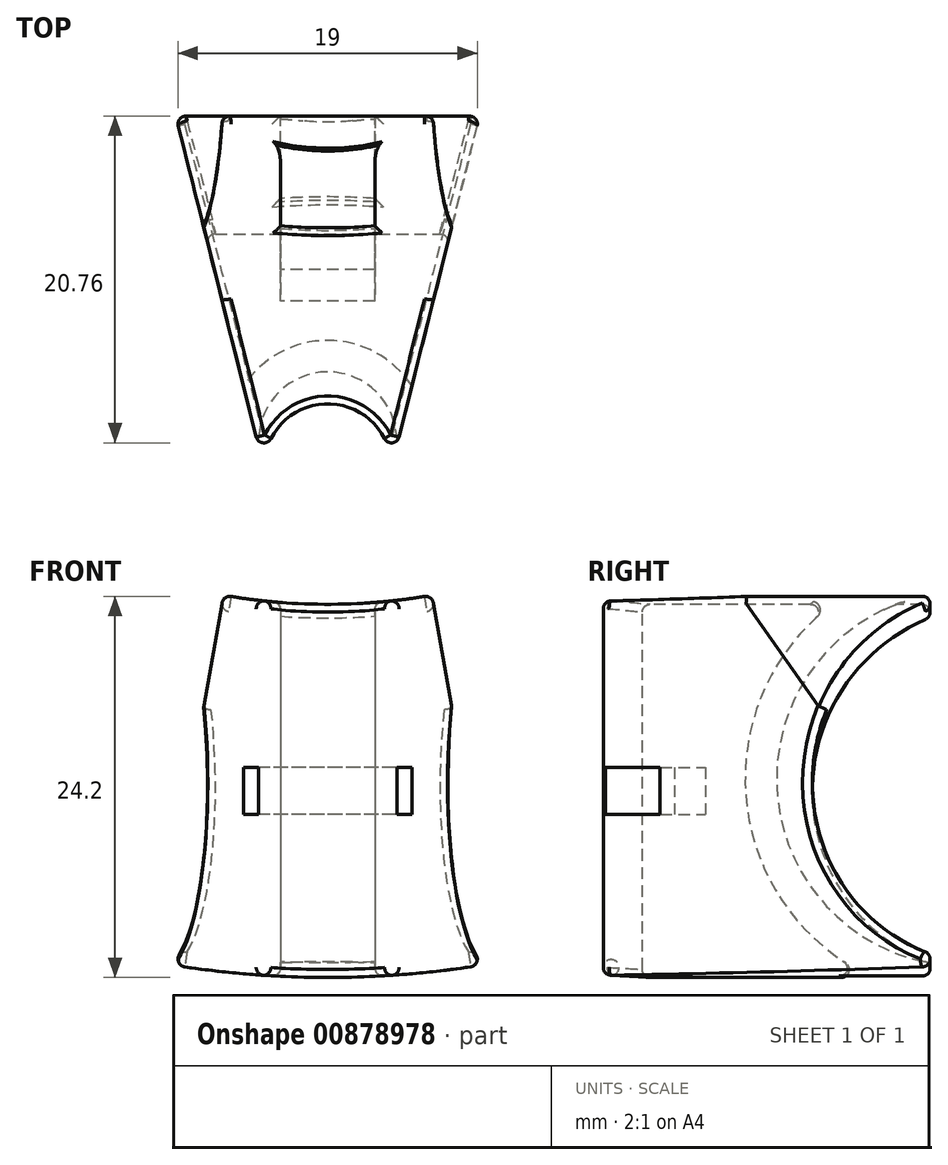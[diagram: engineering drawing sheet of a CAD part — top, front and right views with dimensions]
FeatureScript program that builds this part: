
annotation { "Feature Type Name" : "Feature", "Feature Type Description" : "" }
export const myFeature = defineFeature(function(context is Context, id is Id, definition is map)
    precondition{}
    {
        {
            var Q0;
            Q0=qCreatedBy(makeId("Right.planeOp"),FACE);
            var sketch = newSketch(context, id + "F0", { "sketchPlane" : qUnion([Q0])});
            skLineSegment(sketch, "E0", {"start": v(0, 0) * mm, "end": v(12.73, 0) * mm});
            skLineSegment(sketch, "E1.0", {"start": v(0, -50) * mm, "end": v(12.73, -50) * mm});
            skArc(sketch, "E2", {"start": v(0, -38.15) * mm, "mid": v(-11.85, -50) * mm, "end": v(0, -61.85) * mm});
            skLineSegment(sketch, "E3", {"start": v(0, -38.15) * mm, "end": v(-26.7, -38.15) * mm});
            skLineSegment(sketch, "E4", {"start": v(0, -61.85) * mm, "end": v(-26.7, -61.85) * mm});
            skLineSegment(sketch, "E5", {"start": v(-26.7, -38.15) * mm, "end": v(-26.7, -61.85) * mm});
            skSolve(sketch);
        }
        {
            var Q0;
            Q0 = qSketchRegion(id + "F0", true);
            var Q1;
            Q1=sQuery(id+"F0.wireOp",EDGE,"E0");
            revolve(context, id + "F1", {"surfaceOperationType" : NewSurfaceOperationType.NEW, "entities" : qUnion([Q0]), "axis" : qUnion([Q1]), "revolveType" : RevolveType.SYMMETRIC, "angle" : 20 * degree});
        }
        {
            var Q0;
            Q0=qCreatedBy(makeId("Top.planeOp"),FACE);
            var sketch = newSketch(context, id + "F2", { "sketchPlane" : qUnion([Q0])});
            skLineSegment(sketch, "E6.0", {"start": v(-10.74, -26.7) * mm, "end": v(10.74, -26.7) * mm});
            skCircle(sketch, "E7", {"center": v(0, -26.7) * mm, "radius": 4.05 * mm});
            skSolve(sketch);
        }
        {
            var Q0;
            Q0 = qSketchRegion(id + "F2", true);
            extrude(context, id + "F3", {"entities" : qUnion([Q0]), "operationType" : NewBodyOperationType.REMOVE, "endBound" : BoundingType.THROUGH_ALL, "oppositeDirection" : true, "depth" : 25 * mm, "offsetDistance" : 25 * mm});
        }
        {
            var Q0;
            Q0=qCreatedBy(makeId("Top.planeOp"),FACE);
            var sketch = newSketch(context, id + "F4", { "sketchPlane" : qUnion([Q0])});
            skLineSegment(sketch, "E8.0", {"start": v(-10.74, 0) * mm, "end": v(10.74, 0) * mm});
            skLineSegment(sketch, "E9.0", {"start": v(-10.74, -26.7) * mm, "end": v(-4.05, -26.7) * mm});
            skLineSegment(sketch, "E10.0", {"start": v(4.05, -26.7) * mm, "end": v(10.74, -26.7) * mm});
            skLineSegment(sketch, "E11", {"start": v(-10.74, 0) * mm, "end": v(-4.05, -26.7) * mm});
            skLineSegment(sketch, "E12", {"start": v(4.05, -26.7) * mm, "end": v(10.74, 0) * mm});
            skLineSegment(sketch, "E13", {"start": v(10.74, 0) * mm, "end": v(18.67, 0) * mm});
            skLineSegment(sketch, "E14", {"start": v(18.67, 0) * mm, "end": v(18.67, -26.7) * mm});
            skLineSegment(sketch, "E15", {"start": v(18.67, -26.7) * mm, "end": v(7.4, -26.7) * mm});
            skLineSegment(sketch, "E16", {"start": v(7.4, -26.7) * mm, "end": v(4.05, -26.7) * mm});
            skLineSegment(sketch, "E17", {"start": v(-4.05, -26.7) * mm, "end": v(-16.2, -26.7) * mm});
            skLineSegment(sketch, "E18", {"start": v(-16.2, -26.7) * mm, "end": v(-16.2, 0) * mm});
            skLineSegment(sketch, "E19", {"start": v(-16.2, 0) * mm, "end": v(-10.74, 0) * mm});
            skSolve(sketch);
        }
        {
            var Q0;
            Q0 = qSketchRegion(id + "F4", true);
            extrude(context, id + "F5", {"entities" : qUnion([Q0]), "operationType" : NewBodyOperationType.REMOVE, "endBound" : BoundingType.THROUGH_ALL, "oppositeDirection" : true, "depth" : 25 * mm, "offsetDistance" : 25 * mm});
        }
        {
            var Q0;
            Q0=qCreatedBy(makeId("Right.planeOp"),FACE);
            var sketch = newSketch(context, id + "F6", { "sketchPlane" : qUnion([Q0])});
            skFitSpline(sketch, "E20.0", {"points": [v(0, -60.91) * mm, v(-0.47, -60.93) * mm, v(-1.4, -60.91) * mm, v(-2.56, -60.75) * mm, v(-3.47, -60.54) * mm, v(-4.38, -60.26) * mm, v(-5.46, -59.82) * mm, v(-6.69, -59.13) * mm, v(-7.84, -58.27) * mm, v(-8.86, -57.29) * mm, v(-9.6, -56.36) * mm, v(-10.13, -55.56) * mm, v(-10.6, -54.73) * mm, v(-11, -53.86) * mm, v(-11.32, -52.95) * mm, v(-11.51, -52.25) * mm, v(-11.66, -51.54) * mm, v(-11.8, -50.59) * mm, v(-11.86, -49.63) * mm, v(-11.84, -48.66) * mm, v(-11.75, -47.7) * mm, v(-11.54, -46.51) * mm, v(-11.26, -45.6) * mm, v(-11.1, -45.14) * mm]});
            skEllipticalArc(sketch, "E21.0", {});
            skArc(sketch, "E22", {"start": v(0, -37.57) * mm, "mid": v(-14.12, -49.24) * mm, "end": v(0, -60.91) * mm});
            skArc(sketch, "E23.0", {"start": v(0.38, -35.6) * mm, "mid": v(-16.12, -49.24) * mm, "end": v(0.38, -62.87) * mm});
            skLineSegment(sketch, "E24", {"start": v(0, -60.91) * mm, "end": v(0.38, -62.87) * mm});
            skLineSegment(sketch, "E25", {"start": v(0, -37.57) * mm, "end": v(0.38, -35.6) * mm});
            const initialGuessF6  = {"E21.0": [0, -0.0492403876506104, 1, 0, 0.01185, 0.011669971873194664, 1.5707963267948966, 2.7827175404748377]};
            skSetInitialGuess(sketch, initialGuessF6);
            skSolve(sketch);
        }
        {
            var Q0;
            Q0=makeQuery(id+"F6.imprint","IMPRINT",FACE,{"disambiguationData":[TD([[makeQuery(id+"F6.imprint","IMPRINT",EDGE,{"derivedFrom":sQuery(id+"F6.wireOp",EDGE,"E22")}),-1.0]])]});
            var Q1;
            Q1=sQuery(id+"F6.wireOp",EDGE,"E23.0");
            var Q2;
            Q2=sQuery(id+"F6.wireOp",EDGE,"E22");
            var Q3;
            Q3=sQuery(id+"F6.wireOp",EDGE,"E24");
            var Q4;
            Q4=sQuery(id+"F6.wireOp",EDGE,"E25");
            extrude(context, id + "F7", {"entities" : qUnion([Q0]), "operationType" : NewBodyOperationType.REMOVE, "surfaceEntities" : qUnion([Q1, Q2, Q3, Q4]), "endBound" : BoundingType.SYMMETRIC, "depth" : 6 * mm, "offsetDistance" : 25 * mm});
        }
        {
            var Q0;
            Q0=qCreatedBy(makeId("Top.planeOp"),FACE);
            cPlane(context, id + "F8", {"entities" : qUnion([Q0]), "cplaneType" : CPlaneType.OFFSET, "offset" : 50 * mm, "oppositeDirection" : true, "width" : 150 * mm, "height" : 150 * mm});
        }
        {
            var Q0;
            Q0=qCreatedBy(id+"F8.planeOp",FACE);
            var sketch = newSketch(context, id + "F9", { "sketchPlane" : qUnion([Q0])});
            skArc(sketch, "E26.0", {"start": v(4.05, -26.7) * mm, "mid": v(0, -22.65) * mm, "end": v(-4.05, -26.7) * mm});
            skArc(sketch, "E27", {"start": v(4.05, -26.7) * mm, "mid": v(0, -20.62) * mm, "end": v(-4.05, -26.7) * mm});
            skArc(sketch, "E28.0", {"start": v(5.9, -27.47) * mm, "mid": v(0, -18.62) * mm, "end": v(-5.9, -27.47) * mm});
            skLineSegment(sketch, "E29", {"start": v(-4.05, -26.7) * mm, "end": v(-5.9, -27.47) * mm});
            skLineSegment(sketch, "E30", {"start": v(4.05, -26.7) * mm, "end": v(5.9, -27.47) * mm});
            skSolve(sketch);
        }
        {
            var Q0;
            Q0=makeQuery(id+"F9.imprint","IMPRINT",FACE,{"disambiguationData":[TD([[makeQuery(id+"F9.imprint","IMPRINT",EDGE,{"derivedFrom":sQuery(id+"F9.wireOp",EDGE,"E27")}),-1.0]])]});
            extrude(context, id + "F10", {"entities" : qUnion([Q0]), "operationType" : NewBodyOperationType.REMOVE, "endBound" : BoundingType.SYMMETRIC, "depth" : 3 * mm, "offsetDistance" : 25 * mm});
        }
        {
            var Q0;
            Q0=makeQuery(id+"F1.opRevolve","SWEPT_FACE",FACE,{"disambiguationData":[OSD([sQuery(id+"F0.wireOp",EDGE,"E3")])]});
            fillet(context, id + "F11", {"entities" : qUnion([Q0]), "tangentPropagation" : true, "radius" : 0.5 * mm, "defaultsChanged" : true, "vertexSettings" : [], "allowEdgeOverflow" : false});
        }
        {
            var Q0;
            Q0=makeQuery(id+"F1.opRevolve","SWEPT_FACE",FACE,{"disambiguationData":[OSD([sQuery(id+"F0.wireOp",EDGE,"E4")])]});
            fillet(context, id + "F12", {"entities" : qUnion([Q0]), "tangentPropagation" : true, "radius" : 0.5 * mm, "defaultsChanged" : true, "vertexSettings" : [], "allowEdgeOverflow" : false});
        }
        {
            var Q0;
            Q0=makeQuery(id+"F3.boolean.opBoolean","COPY",FACE,{"derivedFrom":makeQuery(id+"F3.opExtrude","SWEPT_FACE",FACE,{"disambiguationData":[OSD([sQuery(id+"F2.wireOp",EDGE,"E7")])]})});
            fillet(context, id + "F13", {"entities" : qUnion([Q0]), "tangentPropagation" : true, "radius" : 0.5 * mm, "defaultsChanged" : true, "vertexSettings" : [], "allowEdgeOverflow" : false});
        }
        {
            var Q0;
            Q0=makeQuery(id+"F1.opRevolve","CAP_EDGE",EDGE,{"disambiguationData":[OSD([sQuery(id+"F0.wireOp",EDGE,"E2")])],"isStart":false});
            var Q1;
            Q1=makeQuery(id+"F5.boolean.opBoolean","INTERSECT",EDGE,{"derivedFrom":[makeQuery(id+"F1.opRevolve","SWEPT_FACE",FACE,{"disambiguationData":[OSD([sQuery(id+"F0.wireOp",EDGE,"E2")])]}),makeQuery(id+"F5.opExtrude","SWEPT_FACE",FACE,{"disambiguationData":[OSD([sQuery(id+"F4.wireOp",EDGE,"E11")])]})]});
            var Q2;
            Q2=makeQuery(id+"F1.opRevolve","CAP_EDGE",EDGE,{"disambiguationData":[OSD([sQuery(id+"F0.wireOp",EDGE,"E2")])],"isStart":true});
            var Q3;
            Q3=makeQuery(id+"F5.boolean.opBoolean","INTERSECT",EDGE,{"derivedFrom":[makeQuery(id+"F1.opRevolve","SWEPT_FACE",FACE,{"disambiguationData":[OSD([sQuery(id+"F0.wireOp",EDGE,"E2")])]}),makeQuery(id+"F5.opExtrude","SWEPT_FACE",FACE,{"disambiguationData":[OSD([sQuery(id+"F4.wireOp",EDGE,"E12")])]})]});
            fillet(context, id + "F14", {"entities" : qUnion([Q0, Q1, Q2, Q3]), "tangentPropagation" : true, "radius" : 0.5 * mm, "defaultsChanged" : true, "vertexSettings" : [], "allowEdgeOverflow" : false});
        }
    });
